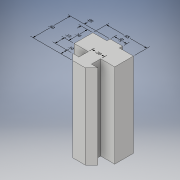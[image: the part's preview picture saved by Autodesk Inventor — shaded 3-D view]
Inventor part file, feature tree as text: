
AUTODESK INVENTOR PART (.ipt)
format: ipt  version: 2018 (Build 220112000, 112)  size: 131,584 bytes
history: native  units: in
note: dims shown in document units (in); Inventor stores cm internally (conversion verified against a paired STEP export)
features: other x9, extrude x1, sketch x1
ambient origin geometry x8: Origin, YZ Plane, XZ Plane, XY Plane, X Axis, Y Axis, Z Axis, Center Point
bodies: Solid1 (feature_tree)
feature tree (11):
  other  "Annotations"
  extrude  "Extrusion1"  Depth=0.3in
  sketch  "Sketch1"  dims[d10=0.65in d11=0.3in d12=0.2in d13=0.6in d18=0.1in d19=0.1in d20=1.35in d21=0.0in d39=0.1301in d40=0.171in d41=0.3in d42=0.3019in d43=0.1444in d44=0.1487in d45=0.0944in d46=0.2217in d47=0.1in d48=0.2719in d49=0.0934in d50=0.6in d51=0.3373in d52=0.0764in d53=0.0513in d54=0.2651in d55=0.1329in d56=0.65in d57=0.1199in d58=0.2in d59=0.1585in d60=0.191in d61=0.2in d22=1.0in d23=1.0in]
  other  "Linear Dimension 1"
  other  "Linear Dimension 2"
  other  "Linear Dimension 3"
  other  "Linear Dimension 4"
  other  "Linear Dimension 5"
  other  "Linear Dimension 6"
  other  "Linear Dimension 7"
  other  "Linear Dimension 8"
